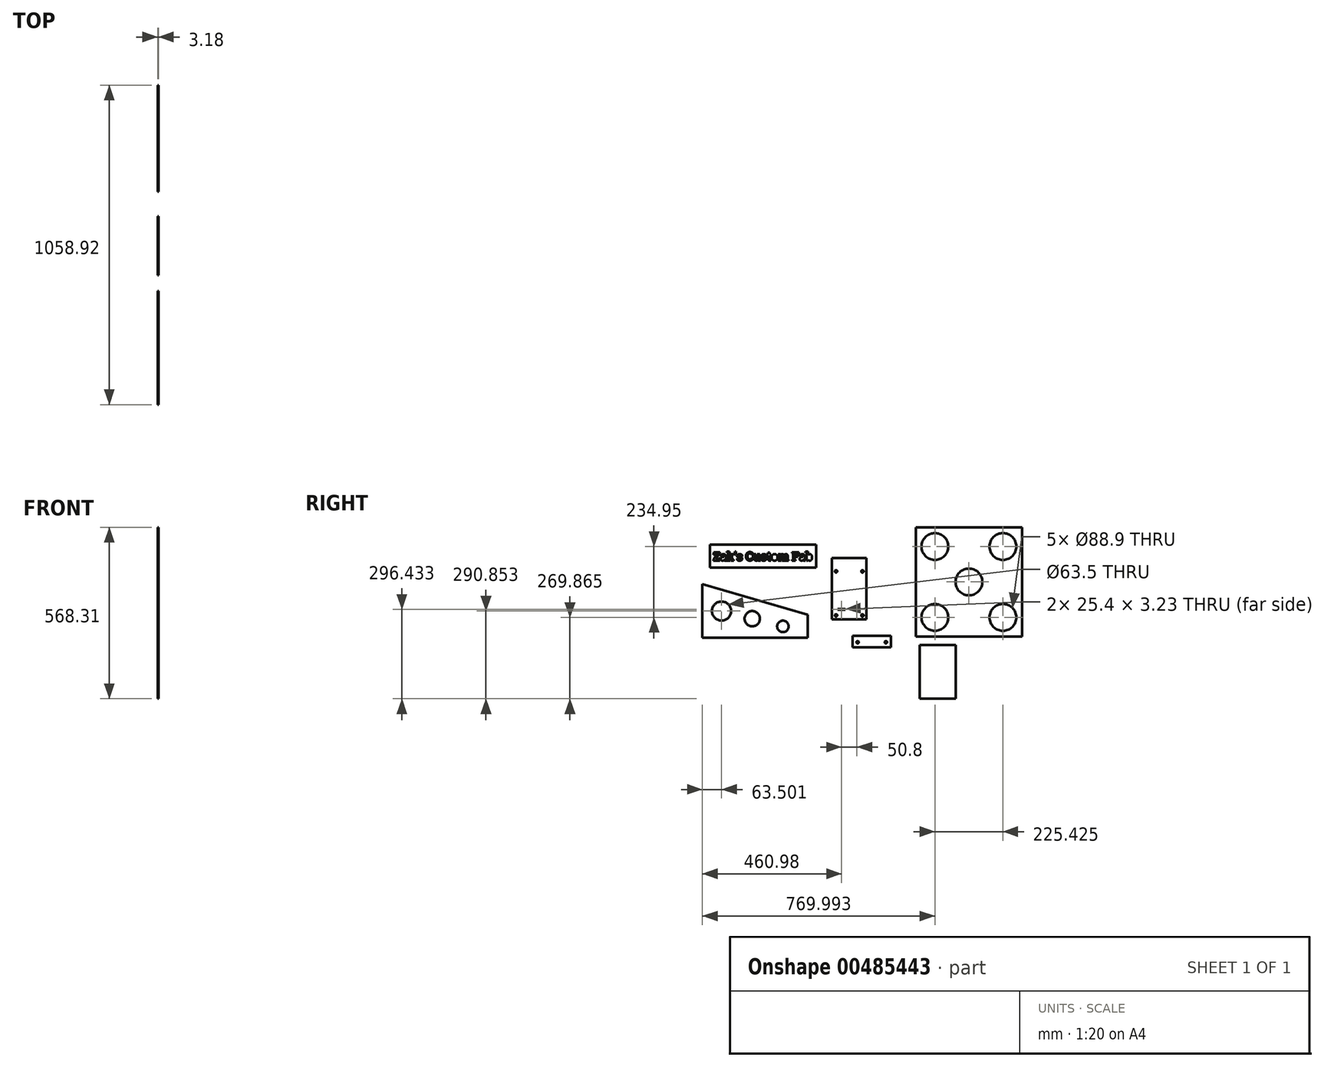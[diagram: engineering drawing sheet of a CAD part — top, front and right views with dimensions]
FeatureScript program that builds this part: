
annotation { "Feature Type Name" : "Feature", "Feature Type Description" : "" }
export const myFeature = defineFeature(function(context is Context, id is Id, definition is map)
    precondition{}
    {
        {
            var Q0;
            Q0=qCreatedBy(makeId("Right.planeOp"),FACE);
            var sketch = newSketch(context, id + "F0", { "sketchPlane" : qUnion([Q0])});
            skLineSegment(sketch, "E0.bottom", {"start": v(-57.15, 101.6) * mm, "end": v(57.15, 101.6) * mm});
            skLineSegment(sketch, "E0.top", {"start": v(-57.15, -101.6) * mm, "end": v(57.15, -101.6) * mm});
            skLineSegment(sketch, "E0.left", {"start": v(-57.15, 101.6) * mm, "end": v(-57.15, -101.6) * mm});
            skLineSegment(sketch, "E0.right", {"start": v(57.15, 101.6) * mm, "end": v(57.15, -101.6) * mm});
            skPoint(sketch, "E0.middle", {"position": v(0, 0) * mm});
            skCircle(sketch, "E1", {"center": v(43.66, 57.94) * mm, "radius": 3.97 * mm});
            skCircle(sketch, "E2", {"center": v(-43.66, 57.94) * mm, "radius": 3.97 * mm});
            skCircle(sketch, "E3", {"center": v(43.66, -88.1) * mm, "radius": 3.97 * mm});
            skCircle(sketch, "E4", {"center": v(-43.66, -88.1) * mm, "radius": 3.97 * mm});
            skLineSegment(sketch, "E5.bottom", {"start": v(38.1, -66.62) * mm, "end": v(12.7, -66.62) * mm});
            skLineSegment(sketch, "E5.top", {"start": v(38.1, -69.85) * mm, "end": v(12.7, -69.85) * mm});
            skLineSegment(sketch, "E5.left", {"start": v(38.1, -66.62) * mm, "end": v(38.1, -69.85) * mm});
            skLineSegment(sketch, "E5.right", {"start": v(12.7, -66.62) * mm, "end": v(12.7, -69.85) * mm});
            skLineSegment(sketch, "E6.bottom", {"start": v(-12.7, -66.62) * mm, "end": v(-38.1, -66.62) * mm});
            skLineSegment(sketch, "E6.top", {"start": v(-12.7, -69.85) * mm, "end": v(-38.1, -69.85) * mm});
            skLineSegment(sketch, "E6.left", {"start": v(-12.7, -66.62) * mm, "end": v(-12.7, -69.85) * mm});
            skLineSegment(sketch, "E6.right", {"start": v(-38.1, -66.62) * mm, "end": v(-38.1, -69.85) * mm});
            skSolve(sketch);
        }
        {
            var Q0;
            Q0=makeQuery(id+"F0.imprint","IMPRINT",FACE,{"disambiguationData":[TD([[makeQuery(id+"F0.imprint","IMPRINT",EDGE,{"derivedFrom":sQuery(id+"F0.wireOp",EDGE,"E0.bottom")}),-1.0]])]});
            extrude(context, id + "F1", {"entities" : qUnion([Q0]), "depth" : 3.17 * mm});
        }
        {
            var Q0;
            Q0=qCreatedBy(makeId("Right.planeOp"),FACE);
            var sketch = newSketch(context, id + "F2", { "sketchPlane" : qUnion([Q0])});
            skLineSegment(sketch, "E7.bottom", {"start": v(138.07, -193.65) * mm, "end": v(11.07, -193.65) * mm});
            skLineSegment(sketch, "E7.top", {"start": v(138.07, -155.55) * mm, "end": v(11.07, -155.55) * mm});
            skLineSegment(sketch, "E7.left", {"start": v(138.07, -193.65) * mm, "end": v(138.07, -155.55) * mm});
            skLineSegment(sketch, "E7.right", {"start": v(11.07, -193.65) * mm, "end": v(11.07, -155.55) * mm});
            skCircle(sketch, "E8", {"center": v(121.4, -176.98) * mm, "radius": 3.97 * mm});
            skCircle(sketch, "E9", {"center": v(27.74, -176.98) * mm, "radius": 3.97 * mm});
            skSolve(sketch);
        }
        {
            var Q0;
            Q0=makeQuery(id+"F2.imprint","IMPRINT",FACE,{"disambiguationData":[TD([[makeQuery(id+"F2.imprint","IMPRINT",EDGE,{"derivedFrom":sQuery(id+"F2.wireOp",EDGE,"E7.bottom")}),-1.0]])]});
            extrude(context, id + "F3", {"entities" : qUnion([Q0]), "depth" : 3.17 * mm});
        }
        {
            var Q0;
            Q0=qCreatedBy(makeId("Right.planeOp"),FACE);
            var sketch = newSketch(context, id + "F4", { "sketchPlane" : qUnion([Q0])});
            skLineSegment(sketch, "E10.bottom", {"start": v(220.11, 203.64) * mm, "end": v(572.54, 203.64) * mm});
            skLineSegment(sketch, "E10.top", {"start": v(220.11, -158.3) * mm, "end": v(572.54, -158.3) * mm});
            skLineSegment(sketch, "E10.left", {"start": v(220.11, 203.64) * mm, "end": v(220.11, -158.3) * mm});
            skLineSegment(sketch, "E10.right", {"start": v(572.54, 203.64) * mm, "end": v(572.54, -158.3) * mm});
            skLineSegment(sketch, "E11.bottom", {"start": v(359.5, 203.64) * mm, "end": v(383.64, 203.64) * mm});
            skLineSegment(sketch, "E11.top", {"start": v(359.5, 206.82) * mm, "end": v(383.64, 206.82) * mm});
            skLineSegment(sketch, "E11.left", {"start": v(359.5, 203.64) * mm, "end": v(359.5, 206.82) * mm});
            skLineSegment(sketch, "E11.right", {"start": v(383.64, 203.64) * mm, "end": v(383.64, 206.82) * mm});
            skLineSegment(sketch, "E12.bottom", {"start": v(409.04, 203.64) * mm, "end": v(433.17, 203.64) * mm});
            skLineSegment(sketch, "E12.top", {"start": v(409.04, 206.82) * mm, "end": v(433.17, 206.82) * mm});
            skLineSegment(sketch, "E12.left", {"start": v(409.04, 203.64) * mm, "end": v(409.04, 206.82) * mm});
            skLineSegment(sketch, "E12.right", {"start": v(433.17, 203.64) * mm, "end": v(433.17, 206.82) * mm});
            skCircle(sketch, "E13", {"center": v(283.61, 140.14) * mm, "radius": 44.45 * mm});
            skCircle(sketch, "E14", {"center": v(509.04, 140.14) * mm, "radius": 44.45 * mm});
            skCircle(sketch, "E15", {"center": v(283.61, -94.8) * mm, "radius": 44.45 * mm});
            skCircle(sketch, "E16", {"center": v(509.04, -94.8) * mm, "radius": 44.45 * mm});
            skCircle(sketch, "E17", {"center": v(396.32, 22.67) * mm, "radius": 44.45 * mm});
            skPoint(sketch, "E17.centerSnap0", {"position": v(220.11, 22.67) * mm});
            skPoint(sketch, "E17.centerSnap1", {"position": v(396.32, -158.3) * mm});
            skSolve(sketch);
        }
        {
            var Q0;
            Q0=makeQuery(id+"F4.imprint","IMPRINT",FACE,{"disambiguationData":[TD([[makeQuery(id+"F4.imprint","IMPRINT",EDGE,{"derivedFrom":sQuery(id+"F4.wireOp",EDGE,"E10.top")}),1.0]])]});
            var Q1;
            Q1=makeQuery(id+"F4.imprint","IMPRINT",FACE,{"disambiguationData":[TD([[makeQuery(id+"F4.imprint","IMPRINT",EDGE,{"derivedFrom":sQuery(id+"F4.wireOp",EDGE,"E11.bottom")}),1.0]])]});
            var Q2;
            Q2=makeQuery(id+"F4.imprint","IMPRINT",FACE,{"disambiguationData":[TD([[makeQuery(id+"F4.imprint","IMPRINT",EDGE,{"derivedFrom":sQuery(id+"F4.wireOp",EDGE,"E12.bottom")}),1.0]])]});
            extrude(context, id + "F5", {"entities" : qUnion([Q0, Q1, Q2]), "depth" : 3.17 * mm});
        }
        {
            var Q0;
            Q0=qCreatedBy(makeId("Right.planeOp"),FACE);
            var sketch = newSketch(context, id + "F6", { "sketchPlane" : qUnion([Q0])});
            skLineSegment(sketch, "E18.bottom", {"start": v(-109.5, 146.81) * mm, "end": v(-461.93, 146.81) * mm});
            skLineSegment(sketch, "E18.top", {"start": v(-109.5, 70.61) * mm, "end": v(-461.93, 70.61) * mm});
            skLineSegment(sketch, "E18.left", {"start": v(-109.5, 146.81) * mm, "end": v(-109.5, 70.61) * mm});
            skLineSegment(sketch, "E18.right", {"start": v(-461.93, 146.81) * mm, "end": v(-461.93, 70.61) * mm});
            skText(sketch, "E19", { "text": "Zak\'s Custom Fab", "fontName": "RobotoSlab-Bold.ttf"});
            const initialGuessF6  = {"E19": [-0.45088, 0.09357, 1, 0, 0.0283]};
            skSetInitialGuess(sketch, initialGuessF6);
            skSolve(sketch);
        }
        {
            var Q0;
            Q0=makeQuery(id+"F6.imprint","IMPRINT",FACE,{"disambiguationData":[TD([[makeQuery(id+"F6.imprint","IMPRINT",EDGE,{"derivedFrom":sQuery(id+"F6.wireOp",EDGE,"E18.bottom")}),1.0]])]});
            extrude(context, id + "F7", {"entities" : qUnion([Q0]), "depth" : 3.17 * mm});
        }
        {
            var Q0;
            Q0=qCreatedBy(makeId("Right.planeOp"),FACE);
            var sketch = newSketch(context, id + "F8", { "sketchPlane" : qUnion([Q0])});
            skLineSegment(sketch, "E20", {"start": v(-486.38, 15.08) * mm, "end": v(-486.38, -162.72) * mm});
            skLineSegment(sketch, "E21", {"start": v(-486.38, -162.72) * mm, "end": v(-137.13, -162.72) * mm});
            skLineSegment(sketch, "E22", {"start": v(-137.13, -86.52) * mm, "end": v(-137.13, -162.72) * mm});
            skLineSegment(sketch, "E23", {"start": v(-137.13, -86.52) * mm, "end": v(-486.38, 15.08) * mm});
            skCircle(sketch, "E24", {"center": v(-422.88, -73.82) * mm, "radius": 31.75 * mm});
            skPoint(sketch, "E24.centerSnap0", {"position": v(-486.38, -73.82) * mm});
            skCircle(sketch, "E25", {"center": v(-321.28, -99.22) * mm, "radius": 25.4 * mm});
            skCircle(sketch, "E26", {"center": v(-219.68, -124.62) * mm, "radius": 19.05 * mm});
            skSolve(sketch);
        }
        {
            var Q0;
            Q0=makeQuery(id+"F8.imprint","IMPRINT",FACE,{"disambiguationData":[TD([[makeQuery(id+"F8.imprint","IMPRINT",EDGE,{"derivedFrom":sQuery(id+"F8.wireOp",EDGE,"E20")}),1.0]])]});
            extrude(context, id + "F9", {"entities" : qUnion([Q0]), "depth" : 3.17 * mm});
        }
        {
            var Q0;
            Q0=qCreatedBy(makeId("Right.planeOp"),FACE);
            var sketch = newSketch(context, id + "F10", { "sketchPlane" : qUnion([Q0])});
            skLineSegment(sketch, "E27.bottom", {"start": v(352.45, -186.87) * mm, "end": v(233.39, -186.87) * mm});
            skLineSegment(sketch, "E27.top", {"start": v(352.45, -364.67) * mm, "end": v(233.39, -364.67) * mm});
            skLineSegment(sketch, "E27.left", {"start": v(352.45, -186.87) * mm, "end": v(352.45, -364.67) * mm});
            skLineSegment(sketch, "E27.right", {"start": v(233.39, -186.87) * mm, "end": v(233.39, -364.67) * mm});
            skSolve(sketch);
        }
        {
            var Q0;
            Q0=makeQuery(id+"F10.imprint","IMPRINT",FACE,{"disambiguationData":[TD([[makeQuery(id+"F10.imprint","IMPRINT",EDGE,{"derivedFrom":sQuery(id+"F10.wireOp",EDGE,"E27.bottom")}),1.0]])]});
            extrude(context, id + "F11", {"entities" : qUnion([Q0]), "depth" : 3.17 * mm});
        }
    });
